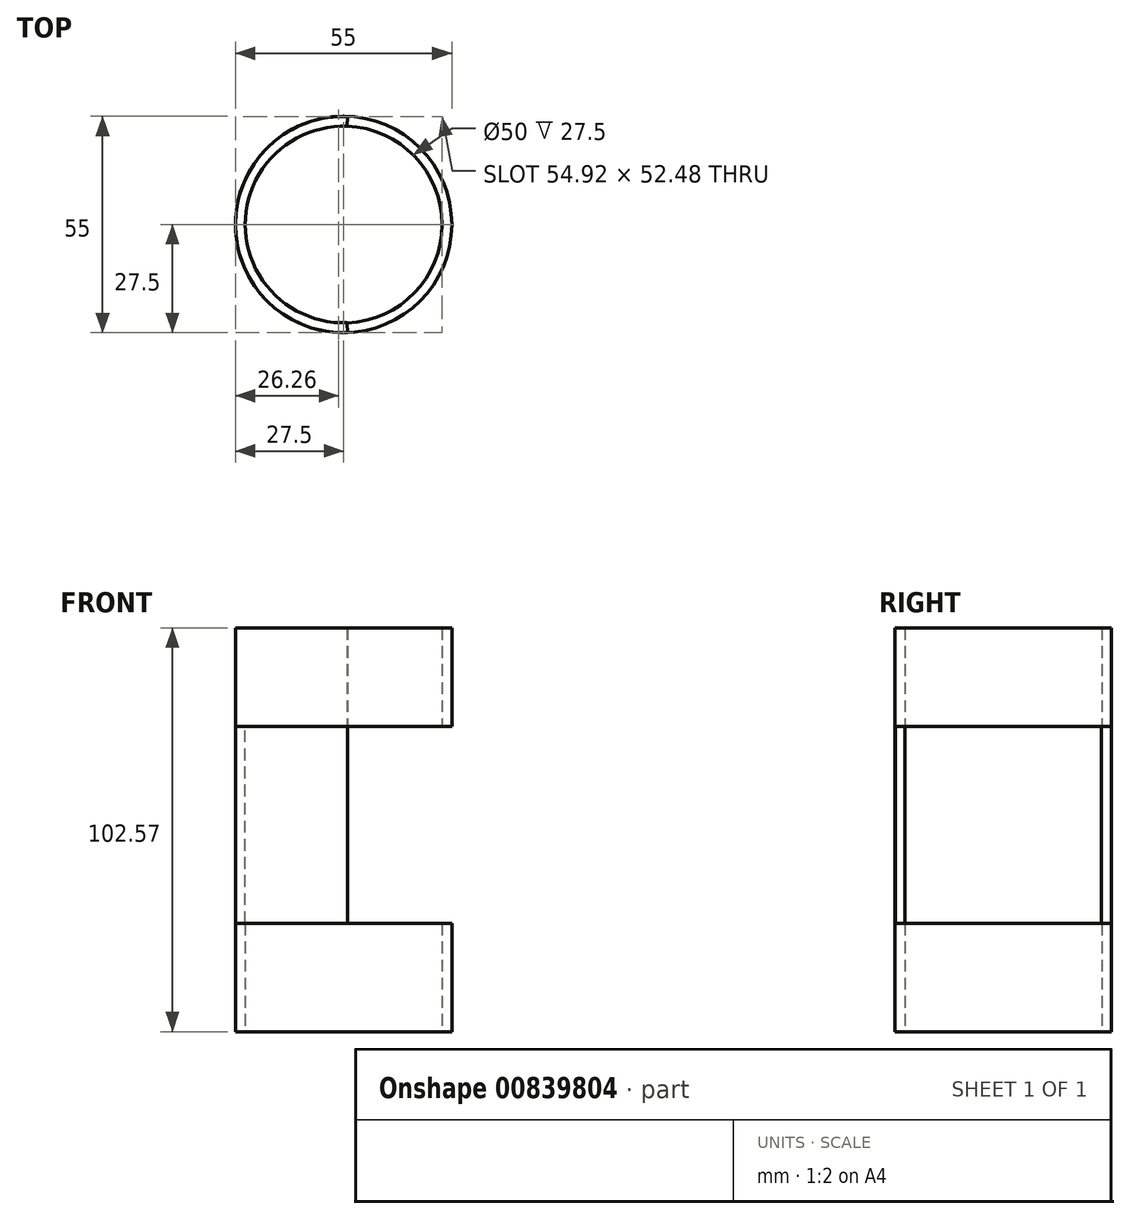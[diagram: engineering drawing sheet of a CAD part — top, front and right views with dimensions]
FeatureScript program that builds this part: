
annotation { "Feature Type Name" : "Feature", "Feature Type Description" : "" }
export const myFeature = defineFeature(function(context is Context, id is Id, definition is map)
    precondition{}
    {
        {
            var Q0;
            Q0=qCreatedBy(makeId("Top.planeOp"),FACE);
            var sketch = newSketch(context, id + "F0", { "sketchPlane" : qUnion([Q0])});
            skCircle(sketch, "E0", {"center": v(0, 0) * mm, "radius": 25 * mm});
            skCircle(sketch, "E1", {"center": v(0, 0) * mm, "radius": 27.5 * mm});
            skSolve(sketch);
        }
        {
            var Q0;
            Q0=makeQuery(id+"F0.imprint","IMPRINT",FACE,{"disambiguationData":[TD([[makeQuery(id+"F0.imprint","IMPRINT",EDGE,{"derivedFrom":sQuery(id+"F0.wireOp",EDGE,"E0")}),-1.0]])]});
            extrude(context, id + "F1", {"entities" : qUnion([Q0]), "depth" : 27.5 * mm, "offsetDistance" : 25 * mm});
        }
        {
            var Q0;
            Q0=qCreatedBy(makeId("Front.planeOp"),FACE);
            var sketch = newSketch(context, id + "F2", { "sketchPlane" : qUnion([Q0])});
            skLineSegment(sketch, "E2.bottom", {"start": v(-27.48, 27.57) * mm, "end": v(-24.98, 27.57) * mm});
            skLineSegment(sketch, "E2.top", {"start": v(-27.48, 77.57) * mm, "end": v(-24.98, 77.57) * mm});
            skLineSegment(sketch, "E2.left", {"start": v(-27.48, 27.57) * mm, "end": v(-27.48, 77.57) * mm});
            skLineSegment(sketch, "E2.right", {"start": v(-24.98, 27.57) * mm, "end": v(-24.98, 77.57) * mm});
            skSolve(sketch);
        }
        {
            var Q0;
            Q0 = qSketchRegion(id + "F2", true);
            var Q1;
            Q1=makeQuery(id+"F1.opExtrude","SWEPT_FACE",FACE,{"disambiguationData":[OSD([sQuery(id+"F0.wireOp",EDGE,"E1")])]});
            revolve(context, id + "F3", {"surfaceOperationType" : NewSurfaceOperationType.NEW, "entities" : qUnion([Q0]), "axis" : qUnion([Q1]), "revolveType" : RevolveType.SYMMETRIC, "angle" : 184.23 * degree});
        }
        {
            var Q0;
            Q0=makeQuery(id+"F3.opRevolve","SWEPT_FACE",FACE,{"disambiguationData":[OSD([sQuery(id+"F2.wireOp",EDGE,"E2.top")])]});
            var sketch = newSketch(context, id + "F4", { "sketchPlane" : qUnion([Q0])});
            skCircle(sketch, "E3", {"center": v(0, 0) * mm, "radius": 25 * mm});
            skCircle(sketch, "E4", {"center": v(0, 0) * mm, "radius": 27.5 * mm});
            skSolve(sketch);
        }
        {
            var Q0;
            Q0=makeQuery(id+"F4.imprint","IMPRINT",FACE,{"disambiguationData":[TD([[makeQuery(id+"F4.imprint","IMPRINT",EDGE,{"derivedFrom":sQuery(id+"F4.wireOp",EDGE,"E4")}),1.0]])]});
            extrude(context, id + "F5", {"entities" : qUnion([Q0]), "operationType" : NewBodyOperationType.ADD, "depth" : 25 * mm, "offsetDistance" : 25 * mm});
        }
    });
